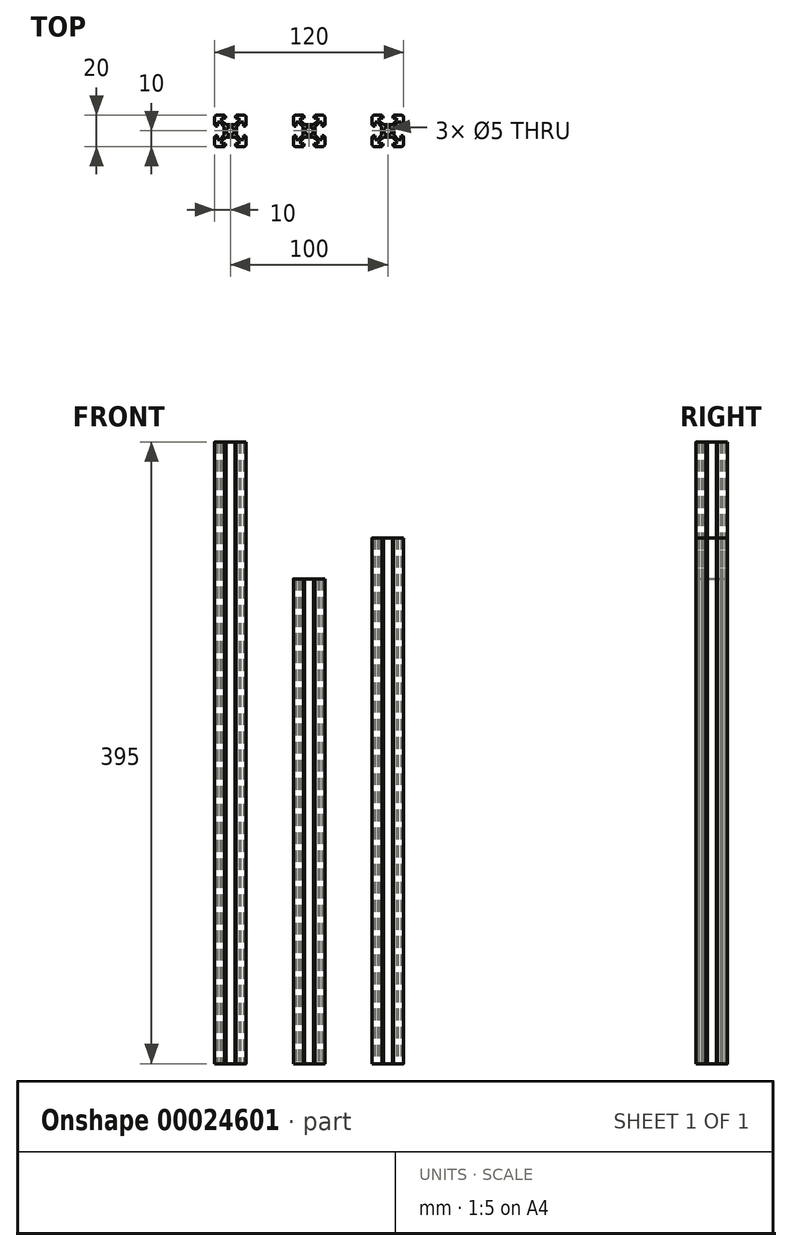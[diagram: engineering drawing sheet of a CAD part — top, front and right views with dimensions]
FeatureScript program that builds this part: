
annotation { "Feature Type Name" : "Feature", "Feature Type Description" : "" }
export const myFeature = defineFeature(function(context is Context, id is Id, definition is map)
    precondition{}
    {
        {
            var Q0;
            Q0=qCreatedBy(makeId("Top.planeOp"),FACE);
            var sketch = newSketch(context, id + "F0", { "sketchPlane" : qUnion([Q0])});
            skLineSegment(sketch, "E0", {"start": v(0, 22.34) * mm, "end": v(0, -25.35) * mm, "construction": true});
            skLineSegment(sketch, "E1", {"start": v(-32.57, 0) * mm, "end": v(34.77, 0) * mm, "construction": true});
            skCircle(sketch, "E2", {"center": v(0, 0) * mm, "radius": 2.5 * mm});
            skLineSegment(sketch, "E3.bottom", {"start": v(0, 0) * mm, "end": v(-10, 0) * mm, "construction": true});
            skLineSegment(sketch, "E3.top", {"start": v(0, 10) * mm, "end": v(-10, 10) * mm, "construction": true});
            skLineSegment(sketch, "E3.left", {"start": v(0, 0) * mm, "end": v(0, 10) * mm, "construction": true});
            skLineSegment(sketch, "E3.right", {"start": v(-10, 0) * mm, "end": v(-10, 10) * mm, "construction": true});
            skLineSegment(sketch, "E4", {"start": v(-10, 10) * mm, "end": v(0, 0) * mm, "construction": true});
            skLineSegment(sketch, "E5", {"start": v(-2.8, 3.9) * mm, "end": v(0, 3.9) * mm});
            skLineSegment(sketch, "E6", {"start": v(-3.65, 10) * mm, "end": v(-8.5, 10) * mm});
            skLineSegment(sketch, "E7", {"start": v(-3.65, 9.5) * mm, "end": v(-3.15, 9.5) * mm});
            skLineSegment(sketch, "E8", {"start": v(-3.15, 9.5) * mm, "end": v(-3.15, 8.2) * mm});
            skLineSegment(sketch, "E9", {"start": v(-3.15, 8.2) * mm, "end": v(-5.5, 8.2) * mm});
            skLineSegment(sketch, "E10", {"start": v(-3.65, 9.5) * mm, "end": v(-3.65, 10) * mm});
            skLineSegment(sketch, "E11", {"start": v(-5.5, 8.2) * mm, "end": v(-5.5, 6.6) * mm});
            skLineSegment(sketch, "E12", {"start": v(-5.5, 6.6) * mm, "end": v(-2.8, 3.9) * mm});
            skLineSegment(sketch, "E13.MirrorCS", {"start": v(3.65, 9.5) * mm, "end": v(3.65, 10) * mm});
            skLineSegment(sketch, "E14.MirrorCS", {"start": v(3.15, 9.5) * mm, "end": v(3.15, 8.2) * mm});
            skLineSegment(sketch, "E15.MirrorCS", {"start": v(3.65, 9.5) * mm, "end": v(3.15, 9.5) * mm});
            skLineSegment(sketch, "E16.MirrorCS", {"start": v(3.15, 8.2) * mm, "end": v(5.5, 8.2) * mm});
            skLineSegment(sketch, "E17.MirrorCS", {"start": v(5.5, 8.2) * mm, "end": v(5.5, 6.6) * mm});
            skLineSegment(sketch, "E18.MirrorCS", {"start": v(5.5, 6.6) * mm, "end": v(2.8, 3.9) * mm});
            skLineSegment(sketch, "E19.MirrorCS", {"start": v(2.8, 3.9) * mm, "end": v(0, 3.9) * mm});
            skLineSegment(sketch, "E20.MirrorCS", {"start": v(-10, 3.65) * mm, "end": v(-10, 8.5) * mm});
            skLineSegment(sketch, "E21.MirrorCS", {"start": v(-9.5, 3.65) * mm, "end": v(-10, 3.65) * mm});
            skLineSegment(sketch, "E22.MirrorCS", {"start": v(-9.5, 3.65) * mm, "end": v(-9.5, 3.15) * mm});
            skLineSegment(sketch, "E23.MirrorCS", {"start": v(-9.5, 3.15) * mm, "end": v(-8.2, 3.15) * mm});
            skLineSegment(sketch, "E24.MirrorCS", {"start": v(-8.2, 3.15) * mm, "end": v(-8.2, 5.5) * mm});
            skLineSegment(sketch, "E25.MirrorCS", {"start": v(-8.2, 5.5) * mm, "end": v(-6.6, 5.5) * mm});
            skLineSegment(sketch, "E26.MirrorCS", {"start": v(-6.6, 5.5) * mm, "end": v(-3.9, 2.8) * mm});
            skLineSegment(sketch, "E27.MirrorCS", {"start": v(-3.9, 2.8) * mm, "end": v(-3.9, 0) * mm});
            skPoint(sketch, "E28.visualSharp", {"position": v(-10, 10) * mm});
            skArc(sketch, "E28.filletArc", {"start": v(-8.5, 10) * mm, "mid": v(-9.56, 9.56) * mm, "end": v(-10, 8.5) * mm});
            skArc(sketch, "E29.MirrorCS", {"start": v(8.5, 10) * mm, "mid": v(9.56, 9.56) * mm, "end": v(10, 8.5) * mm});
            skLineSegment(sketch, "E30.MirrorCS", {"start": v(3.65, 10) * mm, "end": v(8.5, 10) * mm});
            skLineSegment(sketch, "E31.MirrorCS", {"start": v(10, 3.65) * mm, "end": v(10, 8.5) * mm});
            skLineSegment(sketch, "E32.MirrorCS", {"start": v(9.5, 3.65) * mm, "end": v(10, 3.65) * mm});
            skLineSegment(sketch, "E33.MirrorCS", {"start": v(9.5, 3.15) * mm, "end": v(8.2, 3.15) * mm});
            skLineSegment(sketch, "E34.MirrorCS", {"start": v(9.5, 3.65) * mm, "end": v(9.5, 3.15) * mm});
            skLineSegment(sketch, "E35.MirrorCS", {"start": v(8.2, 3.15) * mm, "end": v(8.2, 5.5) * mm});
            skLineSegment(sketch, "E36.MirrorCS", {"start": v(8.2, 5.5) * mm, "end": v(6.6, 5.5) * mm});
            skLineSegment(sketch, "E37.MirrorCS", {"start": v(6.6, 5.5) * mm, "end": v(3.9, 2.8) * mm});
            skLineSegment(sketch, "E38.MirrorCS", {"start": v(3.9, 2.8) * mm, "end": v(3.9, 0) * mm});
            skLineSegment(sketch, "E39.MirrorCS", {"start": v(-3.9, -2.8) * mm, "end": v(-3.9, 0) * mm});
            skLineSegment(sketch, "E40.MirrorCS", {"start": v(-6.6, -5.5) * mm, "end": v(-3.9, -2.8) * mm});
            skLineSegment(sketch, "E41.MirrorCS", {"start": v(-8.2, -5.5) * mm, "end": v(-6.6, -5.5) * mm});
            skLineSegment(sketch, "E42.MirrorCS", {"start": v(-8.2, -3.15) * mm, "end": v(-8.2, -5.5) * mm});
            skLineSegment(sketch, "E43.MirrorCS", {"start": v(-9.5, -3.15) * mm, "end": v(-8.2, -3.15) * mm});
            skLineSegment(sketch, "E44.MirrorCS", {"start": v(-9.5, -3.65) * mm, "end": v(-9.5, -3.15) * mm});
            skLineSegment(sketch, "E45.MirrorCS", {"start": v(-9.5, -3.65) * mm, "end": v(-10, -3.65) * mm});
            skLineSegment(sketch, "E46.MirrorCS", {"start": v(-10, -3.65) * mm, "end": v(-10, -8.5) * mm});
            skArc(sketch, "E47.MirrorCS", {"start": v(-8.5, -10) * mm, "mid": v(-9.56, -9.56) * mm, "end": v(-10, -8.5) * mm});
            skLineSegment(sketch, "E48.MirrorCS", {"start": v(-3.65, -10) * mm, "end": v(-8.5, -10) * mm});
            skLineSegment(sketch, "E49.MirrorCS", {"start": v(-3.65, -9.5) * mm, "end": v(-3.65, -10) * mm});
            skLineSegment(sketch, "E50.MirrorCS", {"start": v(-3.65, -9.5) * mm, "end": v(-3.15, -9.5) * mm});
            skLineSegment(sketch, "E51.MirrorCS", {"start": v(-3.15, -9.5) * mm, "end": v(-3.15, -8.2) * mm});
            skLineSegment(sketch, "E52.MirrorCS", {"start": v(-3.15, -8.2) * mm, "end": v(-5.5, -8.2) * mm});
            skLineSegment(sketch, "E53.MirrorCS", {"start": v(-5.5, -8.2) * mm, "end": v(-5.5, -6.6) * mm});
            skLineSegment(sketch, "E54.MirrorCS", {"start": v(-5.5, -6.6) * mm, "end": v(-2.8, -3.9) * mm});
            skLineSegment(sketch, "E55.MirrorCS", {"start": v(-2.8, -3.9) * mm, "end": v(0, -3.9) * mm});
            skLineSegment(sketch, "E56.MirrorCS", {"start": v(2.8, -3.9) * mm, "end": v(0, -3.9) * mm});
            skLineSegment(sketch, "E57.MirrorCS", {"start": v(3.9, -2.8) * mm, "end": v(3.9, 0) * mm});
            skLineSegment(sketch, "E58.MirrorCS", {"start": v(6.6, -5.5) * mm, "end": v(3.9, -2.8) * mm});
            skLineSegment(sketch, "E59.MirrorCS", {"start": v(8.2, -5.5) * mm, "end": v(6.6, -5.5) * mm});
            skLineSegment(sketch, "E60.MirrorCS", {"start": v(8.2, -3.15) * mm, "end": v(8.2, -5.5) * mm});
            skLineSegment(sketch, "E61.MirrorCS", {"start": v(9.5, -3.15) * mm, "end": v(8.2, -3.15) * mm});
            skLineSegment(sketch, "E62.MirrorCS", {"start": v(9.5, -3.65) * mm, "end": v(10, -3.65) * mm});
            skLineSegment(sketch, "E63.MirrorCS", {"start": v(9.5, -3.65) * mm, "end": v(9.5, -3.15) * mm});
            skLineSegment(sketch, "E64.MirrorCS", {"start": v(10, -3.65) * mm, "end": v(10, -8.5) * mm});
            skLineSegment(sketch, "E65.MirrorCS", {"start": v(3.65, -9.5) * mm, "end": v(3.15, -9.5) * mm});
            skLineSegment(sketch, "E66.MirrorCS", {"start": v(3.65, -9.5) * mm, "end": v(3.65, -10) * mm});
            skLineSegment(sketch, "E67.MirrorCS", {"start": v(3.15, -8.2) * mm, "end": v(5.5, -8.2) * mm});
            skLineSegment(sketch, "E68.MirrorCS", {"start": v(5.5, -8.2) * mm, "end": v(5.5, -6.6) * mm});
            skLineSegment(sketch, "E69.MirrorCS", {"start": v(3.65, -10) * mm, "end": v(8.5, -10) * mm});
            skLineSegment(sketch, "E70.MirrorCS", {"start": v(3.15, -9.5) * mm, "end": v(3.15, -8.2) * mm});
            skArc(sketch, "E71.MirrorCS", {"start": v(8.5, -10) * mm, "mid": v(9.56, -9.56) * mm, "end": v(10, -8.5) * mm});
            skLineSegment(sketch, "E72.MirrorCS", {"start": v(5.5, -6.6) * mm, "end": v(2.8, -3.9) * mm});
            skSolve(sketch);
        }
        {
            var Q0;
            Q0=makeQuery(id+"F0.imprint","IMPRINT",FACE,{"disambiguationData":[TD([[makeQuery(id+"F0.imprint","IMPRINT",EDGE,{"derivedFrom":sQuery(id+"F0.wireOp",EDGE,"E2")}),-1.0]])]});
            extrude(context, id + "F1", {"entities" : qUnion([Q0]), "depth" : 308 * mm});
        }
        {
            var Q0;
            Q0=makeQuery(id+"F1.opExtrude","SWEPT_BODY",BODY,{"disambiguationData":[OSD([sQuery(id+"F0.wireOp",EDGE,"E2"),sQuery(id+"F0.wireOp",EDGE,"E5"),sQuery(id+"F0.wireOp",EDGE,"E6"),sQuery(id+"F0.wireOp",EDGE,"E7"),sQuery(id+"F0.wireOp",EDGE,"E8"),sQuery(id+"F0.wireOp",EDGE,"E9"),sQuery(id+"F0.wireOp",EDGE,"E10"),sQuery(id+"F0.wireOp",EDGE,"E11"),sQuery(id+"F0.wireOp",EDGE,"E12"),sQuery(id+"F0.wireOp",EDGE,"E13.MirrorCS"),sQuery(id+"F0.wireOp",EDGE,"E14.MirrorCS"),sQuery(id+"F0.wireOp",EDGE,"E15.MirrorCS"),sQuery(id+"F0.wireOp",EDGE,"E16.MirrorCS"),sQuery(id+"F0.wireOp",EDGE,"E17.MirrorCS"),sQuery(id+"F0.wireOp",EDGE,"E18.MirrorCS"),sQuery(id+"F0.wireOp",EDGE,"E19.MirrorCS"),sQuery(id+"F0.wireOp",EDGE,"E20.MirrorCS"),sQuery(id+"F0.wireOp",EDGE,"E21.MirrorCS"),sQuery(id+"F0.wireOp",EDGE,"E22.MirrorCS"),sQuery(id+"F0.wireOp",EDGE,"E23.MirrorCS"),sQuery(id+"F0.wireOp",EDGE,"E24.MirrorCS"),sQuery(id+"F0.wireOp",EDGE,"E25.MirrorCS"),sQuery(id+"F0.wireOp",EDGE,"E26.MirrorCS"),sQuery(id+"F0.wireOp",EDGE,"E27.MirrorCS"),sQuery(id+"F0.wireOp",EDGE,"E28.filletArc"),sQuery(id+"F0.wireOp",EDGE,"E29.MirrorCS"),sQuery(id+"F0.wireOp",EDGE,"E30.MirrorCS"),sQuery(id+"F0.wireOp",EDGE,"E31.MirrorCS"),sQuery(id+"F0.wireOp",EDGE,"E32.MirrorCS"),sQuery(id+"F0.wireOp",EDGE,"E33.MirrorCS"),sQuery(id+"F0.wireOp",EDGE,"E34.MirrorCS"),sQuery(id+"F0.wireOp",EDGE,"E35.MirrorCS"),sQuery(id+"F0.wireOp",EDGE,"E36.MirrorCS"),sQuery(id+"F0.wireOp",EDGE,"E37.MirrorCS"),sQuery(id+"F0.wireOp",EDGE,"E38.MirrorCS"),sQuery(id+"F0.wireOp",EDGE,"E39.MirrorCS"),sQuery(id+"F0.wireOp",EDGE,"E40.MirrorCS"),sQuery(id+"F0.wireOp",EDGE,"E41.MirrorCS"),sQuery(id+"F0.wireOp",EDGE,"E42.MirrorCS"),sQuery(id+"F0.wireOp",EDGE,"E43.MirrorCS"),sQuery(id+"F0.wireOp",EDGE,"E44.MirrorCS"),sQuery(id+"F0.wireOp",EDGE,"E45.MirrorCS"),sQuery(id+"F0.wireOp",EDGE,"E46.MirrorCS"),sQuery(id+"F0.wireOp",EDGE,"E47.MirrorCS"),sQuery(id+"F0.wireOp",EDGE,"E48.MirrorCS"),sQuery(id+"F0.wireOp",EDGE,"E49.MirrorCS"),sQuery(id+"F0.wireOp",EDGE,"E50.MirrorCS"),sQuery(id+"F0.wireOp",EDGE,"E51.MirrorCS"),sQuery(id+"F0.wireOp",EDGE,"E52.MirrorCS"),sQuery(id+"F0.wireOp",EDGE,"E53.MirrorCS"),sQuery(id+"F0.wireOp",EDGE,"E54.MirrorCS"),sQuery(id+"F0.wireOp",EDGE,"E55.MirrorCS"),sQuery(id+"F0.wireOp",EDGE,"E56.MirrorCS"),sQuery(id+"F0.wireOp",EDGE,"E57.MirrorCS"),sQuery(id+"F0.wireOp",EDGE,"E58.MirrorCS"),sQuery(id+"F0.wireOp",EDGE,"E59.MirrorCS"),sQuery(id+"F0.wireOp",EDGE,"E60.MirrorCS"),sQuery(id+"F0.wireOp",EDGE,"E61.MirrorCS"),sQuery(id+"F0.wireOp",EDGE,"E62.MirrorCS"),sQuery(id+"F0.wireOp",EDGE,"E63.MirrorCS"),sQuery(id+"F0.wireOp",EDGE,"E65.MirrorCS"),sQuery(id+"F0.wireOp",EDGE,"E66.MirrorCS"),sQuery(id+"F0.wireOp",EDGE,"E64.MirrorCS"),sQuery(id+"F0.wireOp",EDGE,"E67.MirrorCS"),sQuery(id+"F0.wireOp",EDGE,"E68.MirrorCS"),sQuery(id+"F0.wireOp",EDGE,"E69.MirrorCS"),sQuery(id+"F0.wireOp",EDGE,"E70.MirrorCS"),sQuery(id+"F0.wireOp",EDGE,"E71.MirrorCS"),sQuery(id+"F0.wireOp",EDGE,"E72.MirrorCS")])]});
            transform(context, id + "F2", {"entities" : qUnion([Q0]), "transformType" : TransformType.TRANSLATION_3D, "dx" : 50 * mm, "dy" : 0 * mm, "dz" : 0 * mm, "makeCopy" : false});
        }
        {
            var Q0;
            Q0=makeQuery(id+"F0.imprint","IMPRINT",FACE,{"disambiguationData":[TD([[makeQuery(id+"F0.imprint","IMPRINT",EDGE,{"derivedFrom":sQuery(id+"F0.wireOp",EDGE,"E2")}),-1.0]])]});
            extrude(context, id + "F3", {"entities" : qUnion([Q0]), "depth" : 334 * mm});
        }
        {
            var Q0;
            Q0=makeQuery(id+"F3.opExtrude","SWEPT_BODY",BODY,{"disambiguationData":[OSD([sQuery(id+"F0.wireOp",EDGE,"E2"),sQuery(id+"F0.wireOp",EDGE,"E5"),sQuery(id+"F0.wireOp",EDGE,"E6"),sQuery(id+"F0.wireOp",EDGE,"E7"),sQuery(id+"F0.wireOp",EDGE,"E8"),sQuery(id+"F0.wireOp",EDGE,"E9"),sQuery(id+"F0.wireOp",EDGE,"E10"),sQuery(id+"F0.wireOp",EDGE,"E11"),sQuery(id+"F0.wireOp",EDGE,"E12"),sQuery(id+"F0.wireOp",EDGE,"E13.MirrorCS"),sQuery(id+"F0.wireOp",EDGE,"E14.MirrorCS"),sQuery(id+"F0.wireOp",EDGE,"E15.MirrorCS"),sQuery(id+"F0.wireOp",EDGE,"E16.MirrorCS"),sQuery(id+"F0.wireOp",EDGE,"E17.MirrorCS"),sQuery(id+"F0.wireOp",EDGE,"E18.MirrorCS"),sQuery(id+"F0.wireOp",EDGE,"E19.MirrorCS"),sQuery(id+"F0.wireOp",EDGE,"E20.MirrorCS"),sQuery(id+"F0.wireOp",EDGE,"E21.MirrorCS"),sQuery(id+"F0.wireOp",EDGE,"E22.MirrorCS"),sQuery(id+"F0.wireOp",EDGE,"E23.MirrorCS"),sQuery(id+"F0.wireOp",EDGE,"E24.MirrorCS"),sQuery(id+"F0.wireOp",EDGE,"E25.MirrorCS"),sQuery(id+"F0.wireOp",EDGE,"E26.MirrorCS"),sQuery(id+"F0.wireOp",EDGE,"E27.MirrorCS"),sQuery(id+"F0.wireOp",EDGE,"E28.filletArc"),sQuery(id+"F0.wireOp",EDGE,"E29.MirrorCS"),sQuery(id+"F0.wireOp",EDGE,"E30.MirrorCS"),sQuery(id+"F0.wireOp",EDGE,"E31.MirrorCS"),sQuery(id+"F0.wireOp",EDGE,"E32.MirrorCS"),sQuery(id+"F0.wireOp",EDGE,"E33.MirrorCS"),sQuery(id+"F0.wireOp",EDGE,"E34.MirrorCS"),sQuery(id+"F0.wireOp",EDGE,"E35.MirrorCS"),sQuery(id+"F0.wireOp",EDGE,"E36.MirrorCS"),sQuery(id+"F0.wireOp",EDGE,"E37.MirrorCS"),sQuery(id+"F0.wireOp",EDGE,"E38.MirrorCS"),sQuery(id+"F0.wireOp",EDGE,"E39.MirrorCS"),sQuery(id+"F0.wireOp",EDGE,"E40.MirrorCS"),sQuery(id+"F0.wireOp",EDGE,"E41.MirrorCS"),sQuery(id+"F0.wireOp",EDGE,"E42.MirrorCS"),sQuery(id+"F0.wireOp",EDGE,"E43.MirrorCS"),sQuery(id+"F0.wireOp",EDGE,"E44.MirrorCS"),sQuery(id+"F0.wireOp",EDGE,"E45.MirrorCS"),sQuery(id+"F0.wireOp",EDGE,"E46.MirrorCS"),sQuery(id+"F0.wireOp",EDGE,"E47.MirrorCS"),sQuery(id+"F0.wireOp",EDGE,"E48.MirrorCS"),sQuery(id+"F0.wireOp",EDGE,"E49.MirrorCS"),sQuery(id+"F0.wireOp",EDGE,"E50.MirrorCS"),sQuery(id+"F0.wireOp",EDGE,"E51.MirrorCS"),sQuery(id+"F0.wireOp",EDGE,"E52.MirrorCS"),sQuery(id+"F0.wireOp",EDGE,"E53.MirrorCS"),sQuery(id+"F0.wireOp",EDGE,"E54.MirrorCS"),sQuery(id+"F0.wireOp",EDGE,"E55.MirrorCS"),sQuery(id+"F0.wireOp",EDGE,"E56.MirrorCS"),sQuery(id+"F0.wireOp",EDGE,"E57.MirrorCS"),sQuery(id+"F0.wireOp",EDGE,"E58.MirrorCS"),sQuery(id+"F0.wireOp",EDGE,"E59.MirrorCS"),sQuery(id+"F0.wireOp",EDGE,"E60.MirrorCS"),sQuery(id+"F0.wireOp",EDGE,"E61.MirrorCS"),sQuery(id+"F0.wireOp",EDGE,"E62.MirrorCS"),sQuery(id+"F0.wireOp",EDGE,"E63.MirrorCS"),sQuery(id+"F0.wireOp",EDGE,"E65.MirrorCS"),sQuery(id+"F0.wireOp",EDGE,"E66.MirrorCS"),sQuery(id+"F0.wireOp",EDGE,"E64.MirrorCS"),sQuery(id+"F0.wireOp",EDGE,"E67.MirrorCS"),sQuery(id+"F0.wireOp",EDGE,"E68.MirrorCS"),sQuery(id+"F0.wireOp",EDGE,"E69.MirrorCS"),sQuery(id+"F0.wireOp",EDGE,"E70.MirrorCS"),sQuery(id+"F0.wireOp",EDGE,"E71.MirrorCS"),sQuery(id+"F0.wireOp",EDGE,"E72.MirrorCS")])]});
            transform(context, id + "F4", {"entities" : qUnion([Q0]), "transformType" : TransformType.TRANSLATION_3D, "dx" : 100 * mm, "dy" : 0 * mm, "dz" : 0 * mm, "makeCopy" : false});
        }
        {
            var Q0;
            Q0=makeQuery(id+"F0.imprint","IMPRINT",FACE,{"disambiguationData":[TD([[makeQuery(id+"F0.imprint","IMPRINT",EDGE,{"derivedFrom":sQuery(id+"F0.wireOp",EDGE,"E2")}),-1.0]])]});
            extrude(context, id + "F5", {"entities" : qUnion([Q0]), "depth" : 395 * mm});
        }
    });
